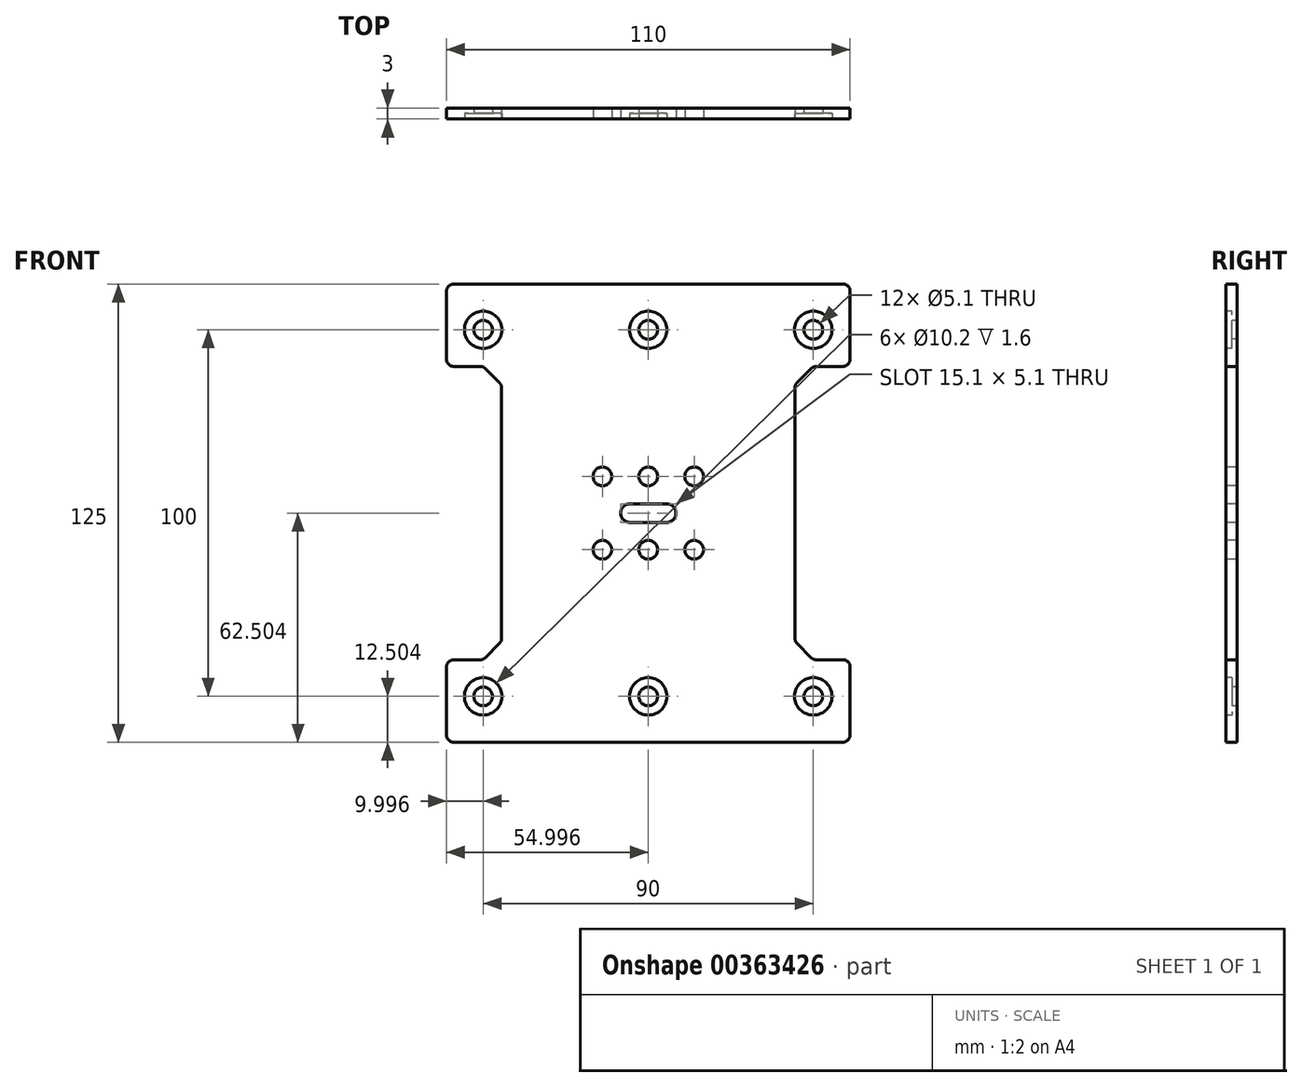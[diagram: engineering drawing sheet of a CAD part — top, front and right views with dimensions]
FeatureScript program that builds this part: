
annotation { "Feature Type Name" : "Feature", "Feature Type Description" : "" }
export const myFeature = defineFeature(function(context is Context, id is Id, definition is map)
    precondition{}
    {
        {
            var Q0;
            Q0=qCreatedBy(makeId("Front.planeOp"),FACE);
            var sketch = newSketch(context, id + "F0", { "sketchPlane" : qUnion([Q0])});
            skLineSegment(sketch, "E0", {"start": v(-210.77, 89) * mm, "end": v(-157.77, 89) * mm});
            skPoint(sketch, "E1", {"position": v(-40, -339.13) * mm});
            skLineSegment(sketch, "E2", {"start": v(-197.77, 26.5) * mm, "end": v(-197.77, 60.75) * mm});
            skLineSegment(sketch, "E3", {"start": v(-203.52, 66.5) * mm, "end": v(-210.77, 66.5) * mm});
            skLineSegment(sketch, "E4", {"start": v(-212.77, 68.5) * mm, "end": v(-212.77, 87) * mm});
            skLineSegment(sketch, "E5", {"start": v(-212.77, 76.5) * mm, "end": v(-157.77, 76.5) * mm, "construction": true});
            skLineSegment(sketch, "E6", {"start": v(-157.77, 89) * mm, "end": v(-157.77, 29.04) * mm});
            skPoint(sketch, "E7", {"position": v(-157.77, 76.5) * mm});
            skPoint(sketch, "E8", {"position": v(-202.77, 76.5) * mm});
            skLineSegment(sketch, "E9", {"start": v(-170.27, 89) * mm, "end": v(-170.27, 26.5) * mm, "construction": true});
            skLineSegment(sketch, "E10", {"start": v(-197.77, 26.5) * mm, "end": v(-165.32, 26.5) * mm});
            skPoint(sketch, "E11", {"position": v(-170.27, 36.5) * mm});
            skLineSegment(sketch, "E12", {"start": v(-202.25, 65.97) * mm, "end": v(-198.3, 62.02) * mm});
            skPoint(sketch, "E13.visualSharp", {"position": v(-212.77, 66.5) * mm});
            skArc(sketch, "E13.filletArc", {"start": v(-212.77, 68.5) * mm, "mid": v(-212.19, 67.08) * mm, "end": v(-210.77, 66.5) * mm});
            skPoint(sketch, "E14.newPointB", {"position": v(-202.7, 66.41) * mm});
            skArc(sketch, "E14.filletArc", {"start": v(-202.25, 65.97) * mm, "mid": v(-202.83, 66.36) * mm, "end": v(-203.52, 66.5) * mm});
            skPoint(sketch, "E15.newPointB", {"position": v(-197.77, 66.7) * mm});
            skArc(sketch, "E15.filletArc", {"start": v(-197.77, 60.75) * mm, "mid": v(-197.91, 61.44) * mm, "end": v(-198.3, 62.02) * mm});
            skPoint(sketch, "E16.visualSharp", {"position": v(-212.77, 89) * mm});
            skArc(sketch, "E16.filletArc", {"start": v(-210.77, 89) * mm, "mid": v(-212.19, 88.4) * mm, "end": v(-212.77, 87) * mm});
            skPoint(sketch, "E17", {"position": v(-157.77, 36.5) * mm});
            skPoint(sketch, "E18", {"position": v(-162.77, 26.5) * mm});
            skPoint(sketch, "E19", {"position": v(-157.77, 29.04) * mm});
            skPoint(sketch, "E20", {"position": v(-162.77, 29.04) * mm});
            skLineSegment(sketch, "E21", {"start": v(-157.77, 29.04) * mm, "end": v(-162.77, 29.04) * mm});
            skPoint(sketch, "E22.orphan", {"position": v(-157.77, 26.5) * mm});
            skArc(sketch, "E23", {"start": v(-162.77, 29.04) * mm, "mid": v(-164.58, 28.3) * mm, "end": v(-165.32, 26.5) * mm});
            skSolve(sketch);
        }
        {
            var Q0;
            Q0=makeQuery(id+"F0.imprint","IMPRINT",FACE,{"disambiguationData":[TD([[makeQuery(id+"F0.imprint","IMPRINT",EDGE,{"derivedFrom":sQuery(id+"F0.wireOp",EDGE,"E0")}),-1.0]])]});
            extrude(context, id + "F1", {"entities" : qUnion([Q0]), "oppositeDirection" : true, "depth" : 3 * mm});
        }
        {
            var Q0;
            Q0=sQuery(id+"F0.wireOp",VERTEX,"fb37573f-1244-4946-bf74-be58a5af1915");
            var Q1;
            Q1=sQuery(id+"F0.wireOp",VERTEX,"c7024e13-609b-4777-bc21-ca571d30c209");
            var Q2;
            Q2=sQuery(id+"F0.wireOp",VERTEX,"E11");
            var Q3;
            Q3=makeQuery(id+"F1.opExtrude","SWEPT_BODY",BODY,{"disambiguationData":[OSD([sQuery(id+"F0.wireOp",EDGE,"E0"),sQuery(id+"F0.wireOp",EDGE,"E2"),sQuery(id+"F0.wireOp",EDGE,"E3"),sQuery(id+"F0.wireOp",EDGE,"E4"),sQuery(id+"F0.wireOp",EDGE,"E6"),sQuery(id+"F0.wireOp",EDGE,"E10"),sQuery(id+"F0.wireOp",EDGE,"E12"),sQuery(id+"F0.wireOp",EDGE,"E13.filletArc"),sQuery(id+"F0.wireOp",EDGE,"E14.filletArc"),sQuery(id+"F0.wireOp",EDGE,"E15.filletArc"),sQuery(id+"F0.wireOp",EDGE,"E16.filletArc")])]});
            hole(context, id + "F2", {"style" : HoleStyle.SIMPLE, "endStyle" : HoleEndStyle.BLIND, "holeDiameter" : 5.1 * mm, "holeDepth" : 34.5 * mm, "isTappedThrough" : true, "tappedDepth" : 30 * mm, "tapClearance" : 3, "startFromSketch" : true, "locations" : qUnion([Q0, Q1, Q2]), "scope" : qUnion([Q3])});
        }
        {
            var Q0;
            Q0=sQuery(id+"F0.wireOp",VERTEX,"E8");
            var Q1;
            Q1=makeQuery(id+"F1.opExtrude","SWEPT_BODY",BODY,{"disambiguationData":[OSD([sQuery(id+"F0.wireOp",EDGE,"E0"),sQuery(id+"F0.wireOp",EDGE,"E2"),sQuery(id+"F0.wireOp",EDGE,"E3"),sQuery(id+"F0.wireOp",EDGE,"E4"),sQuery(id+"F0.wireOp",EDGE,"E6"),sQuery(id+"F0.wireOp",EDGE,"E10"),sQuery(id+"F0.wireOp",EDGE,"E12"),sQuery(id+"F0.wireOp",EDGE,"E13.filletArc"),sQuery(id+"F0.wireOp",EDGE,"E14.filletArc"),sQuery(id+"F0.wireOp",EDGE,"E15.filletArc"),sQuery(id+"F0.wireOp",EDGE,"E16.filletArc")])]});
            hole(context, id + "F3", {"style" : HoleStyle.C_BORE, "endStyle" : HoleEndStyle.BLIND, "holeDiameter" : 5.1 * mm, "cBoreDiameter" : 10.2 * mm, "cBoreDepth" : 1.6 * mm, "holeDepth" : 34.5 * mm, "isTappedThrough" : true, "tappedDepth" : 30 * mm, "tapClearance" : 3, "startFromSketch" : true, "locations" : qUnion([Q0]), "scope" : qUnion([Q1])});
        }
        {
            var Q0;
            Q0=makeQuery(id+"F1.opExtrude","SWEPT_BODY",BODY,{"disambiguationData":[OSD([sQuery(id+"F0.wireOp",EDGE,"E0"),sQuery(id+"F0.wireOp",EDGE,"E2"),sQuery(id+"F0.wireOp",EDGE,"E3"),sQuery(id+"F0.wireOp",EDGE,"E4"),sQuery(id+"F0.wireOp",EDGE,"E6"),sQuery(id+"F0.wireOp",EDGE,"E10"),sQuery(id+"F0.wireOp",EDGE,"E12"),sQuery(id+"F0.wireOp",EDGE,"E13.filletArc"),sQuery(id+"F0.wireOp",EDGE,"E14.filletArc"),sQuery(id+"F0.wireOp",EDGE,"E15.filletArc"),sQuery(id+"F0.wireOp",EDGE,"E16.filletArc")])]});
            var Q1;
            Q1=makeQuery(id+"F1.opExtrude","SWEPT_FACE",FACE,{"disambiguationData":[OSD([sQuery(id+"F0.wireOp",EDGE,"E6")])]});
            mirror(context, id + "F4", {"operationType" : NewBodyOperationType.ADD, "entities" : qUnion([Q0]), "mirrorPlane" : qUnion([Q1])});
        }
        {
            var Q0;
            Q0=sQuery(id+"F0.wireOp",VERTEX,"E17");
            var Q1;
            Q1=makeQuery(id+"F1.opExtrude","SWEPT_BODY",BODY,{"disambiguationData":[OSD([sQuery(id+"F0.wireOp",EDGE,"E0"),sQuery(id+"F0.wireOp",EDGE,"E2"),sQuery(id+"F0.wireOp",EDGE,"E3"),sQuery(id+"F0.wireOp",EDGE,"E4"),sQuery(id+"F0.wireOp",EDGE,"E6"),sQuery(id+"F0.wireOp",EDGE,"E10"),sQuery(id+"F0.wireOp",EDGE,"E12"),sQuery(id+"F0.wireOp",EDGE,"E13.filletArc"),sQuery(id+"F0.wireOp",EDGE,"E14.filletArc"),sQuery(id+"F0.wireOp",EDGE,"E15.filletArc"),sQuery(id+"F0.wireOp",EDGE,"E16.filletArc"),sQuery(id+"F0.wireOp",EDGE,"E21"),sQuery(id+"F0.wireOp",EDGE,"E23")])]});
            hole(context, id + "F5", {"style" : HoleStyle.SIMPLE, "endStyle" : HoleEndStyle.BLIND, "holeDiameter" : 5.1 * mm, "holeDepth" : 34.5 * mm, "isTappedThrough" : true, "tappedDepth" : 30 * mm, "tapClearance" : 3, "startFromSketch" : true, "locations" : qUnion([Q0]), "scope" : qUnion([Q1])});
        }
        {
            var Q0;
            Q0=sQuery(id+"F0.wireOp",VERTEX,"E7");
            var Q1;
            Q1=makeQuery(id+"F1.opExtrude","SWEPT_BODY",BODY,{"disambiguationData":[OSD([sQuery(id+"F0.wireOp",EDGE,"E0"),sQuery(id+"F0.wireOp",EDGE,"E2"),sQuery(id+"F0.wireOp",EDGE,"E3"),sQuery(id+"F0.wireOp",EDGE,"E4"),sQuery(id+"F0.wireOp",EDGE,"E6"),sQuery(id+"F0.wireOp",EDGE,"E10"),sQuery(id+"F0.wireOp",EDGE,"E12"),sQuery(id+"F0.wireOp",EDGE,"E13.filletArc"),sQuery(id+"F0.wireOp",EDGE,"E14.filletArc"),sQuery(id+"F0.wireOp",EDGE,"E15.filletArc"),sQuery(id+"F0.wireOp",EDGE,"E16.filletArc")])]});
            hole(context, id + "F6", {"style" : HoleStyle.C_BORE, "endStyle" : HoleEndStyle.BLIND, "holeDiameter" : 5.1 * mm, "cBoreDiameter" : 10.2 * mm, "cBoreDepth" : 1.6 * mm, "holeDepth" : 34.5 * mm, "isTappedThrough" : true, "tappedDepth" : 30 * mm, "tapClearance" : 3, "startFromSketch" : true, "locations" : qUnion([Q0]), "scope" : qUnion([Q1])});
        }
        {
            var Q0;
            Q0=makeQuery(id+"F1.opExtrude","SWEPT_BODY",BODY,{"disambiguationData":[OSD([sQuery(id+"F0.wireOp",EDGE,"E0"),sQuery(id+"F0.wireOp",EDGE,"E2"),sQuery(id+"F0.wireOp",EDGE,"E3"),sQuery(id+"F0.wireOp",EDGE,"E4"),sQuery(id+"F0.wireOp",EDGE,"E6"),sQuery(id+"F0.wireOp",EDGE,"E10"),sQuery(id+"F0.wireOp",EDGE,"E12"),sQuery(id+"F0.wireOp",EDGE,"E13.filletArc"),sQuery(id+"F0.wireOp",EDGE,"E14.filletArc"),sQuery(id+"F0.wireOp",EDGE,"E15.filletArc"),sQuery(id+"F0.wireOp",EDGE,"E16.filletArc")])]});
            var Q1;
            Q1=makeQuery(id+"F1.opExtrude","SWEPT_FACE",FACE,{"disambiguationData":[OSD([sQuery(id+"F0.wireOp",EDGE,"E10")])]});
            mirror(context, id + "F7", {"operationType" : NewBodyOperationType.ADD, "entities" : qUnion([Q0]), "mirrorPlane" : qUnion([Q1])});
        }
    });
